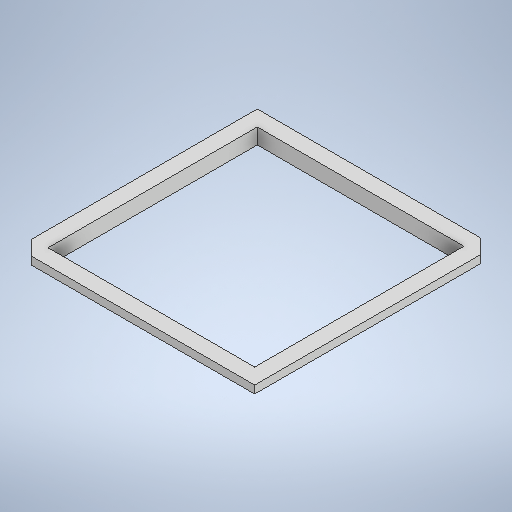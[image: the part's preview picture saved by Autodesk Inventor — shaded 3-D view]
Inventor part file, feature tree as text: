
AUTODESK INVENTOR PART (.ipt)
format: ipt  version: 2025 (Build 290162000, 162)  size: 295,424 bytes
history: native  units: mm
features: extrude x4, sketch x4, chamfer x2
ambient origin geometry x8: Origin, YZ Plane, XZ Plane, XY Plane, X Axis, Y Axis, Z Axis, Center Point
bodies: Solid1 (feature_tree)
feature tree (10):
  extrude  "Extrusion1"  Depth=42.8mm
  extrude  "Extrusion2"  Depth=1.5mm
  extrude  "Extrusion3"  Depth=1.5mm TaperAngle=0.0deg
  chamfer  "Chamfer1"  Distance=1.5mm
  extrude  "Extrusion4"  TaperAngle=0.0deg  [1 undecoded]
  chamfer  "Chamfer2"  Distance=2.9mm Angle=45.0deg
  sketch  "Sketch1"  dims[d0=43.3mm d1=42.8mm]
  sketch  "Sketch2"  dims[d2=1.5mm d3=0.0mm d4=1.5mm]
  sketch  "Sketch3"  dims[d5=1.5mm d6=1.5mm d7=0.0mm]
  sketch  "Sketch4"  dims[d8=1.5mm d9=1.5mm d10=0.0mm d11=0.0mm d12=2.9mm d13=2.0mm d14=45.0deg d16=44.8mm d17=22.4mm d18=0.75mm d19=10.0mm d20=0.0mm d21=0.5mm d22=2.0mm d23=45.0deg]
note: 1 required parameter value undecoded (feature->parameter linkage not recoverable at this tier; creation-order binding heuristic only, values carry confidence <= 0.55)
